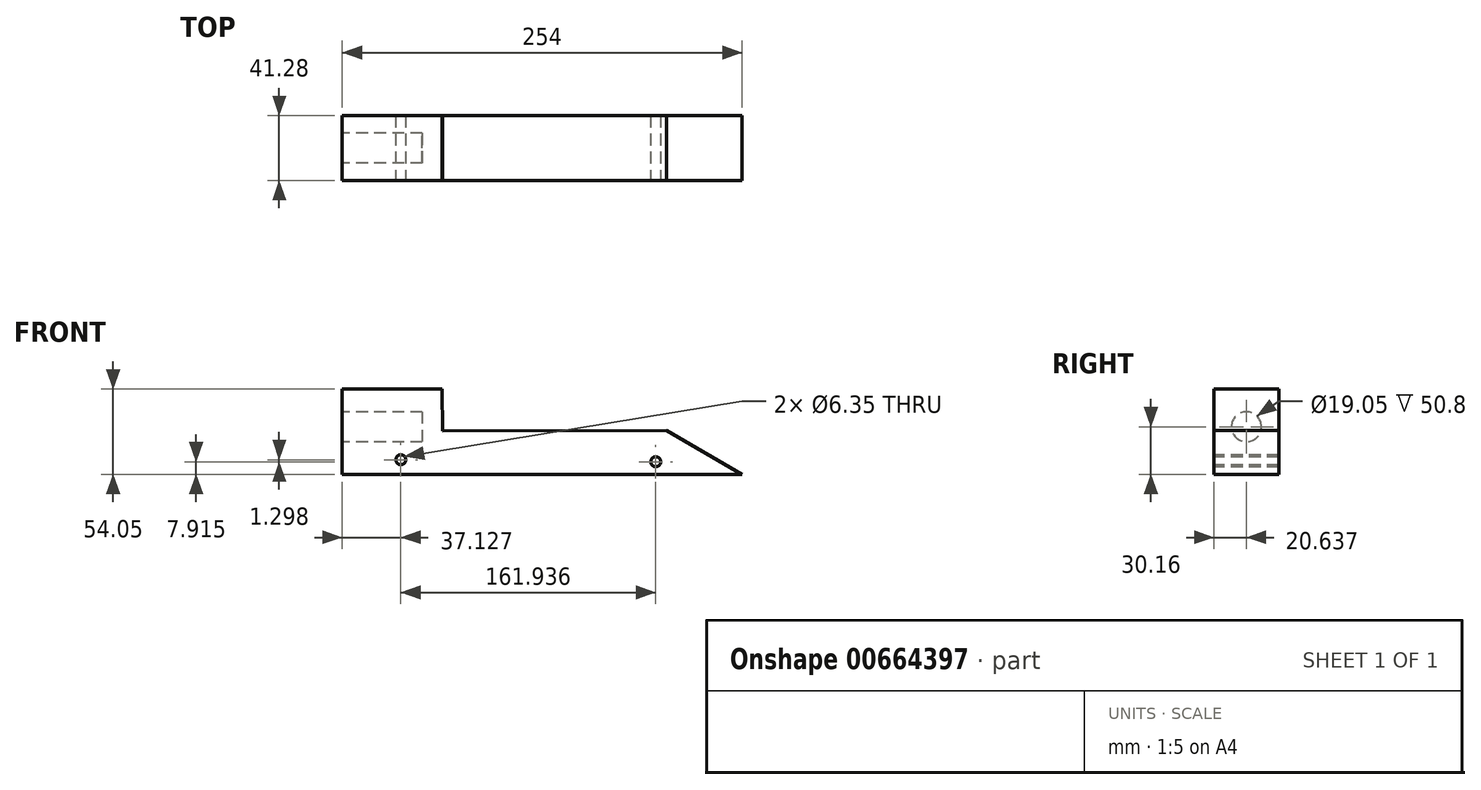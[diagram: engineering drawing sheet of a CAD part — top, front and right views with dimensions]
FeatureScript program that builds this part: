
annotation { "Feature Type Name" : "Feature", "Feature Type Description" : "" }
export const myFeature = defineFeature(function(context is Context, id is Id, definition is map)
    precondition{}
    {
        {
            var Q0;
            Q0=qCreatedBy(makeId("Front.planeOp"),FACE);
            var sketch = newSketch(context, id + "F0", { "sketchPlane" : qUnion([Q0])});
            skLineSegment(sketch, "E0", {"start": v(0, 73.03) * mm, "end": v(0, 0) * mm});
            skLineSegment(sketch, "E1", {"start": v(0, 0) * mm, "end": v(304.8, 0) * mm});
            skLineSegment(sketch, "E2", {"start": v(304.8, 0) * mm, "end": v(304.8, 19.05) * mm});
            skLineSegment(sketch, "E3", {"start": v(304.8, 19.05) * mm, "end": v(0, 73.03) * mm});
            skSolve(sketch);
        }
        {
            var Q0;
            Q0=makeQuery(id+"F0.imprint","IMPRINT",FACE,{"disambiguationData":[TD([[makeQuery(id+"F0.imprint","IMPRINT",EDGE,{"derivedFrom":sQuery(id+"F0.wireOp",EDGE,"E0")}),1.0]])]});
            extrude(context, id + "F1", {"entities" : qUnion([Q0]), "oppositeDirection" : true, "depth" : 41.27 * mm, "offsetDistance" : 25.4 * mm});
        }
        {
            var Q0;
            Q0=makeQuery(id+"F1.opExtrude","SWEPT_FACE",FACE,{"disambiguationData":[OSD([sQuery(id+"F0.wireOp",EDGE,"E0")])]});
            var sketch = newSketch(context, id + "F2", { "sketchPlane" : qUnion([Q0])});
            skCircle(sketch, "E4", {"center": v(-20.64, 30.16) * mm, "radius": 9.53 * mm});
            skSolve(sketch);
        }
        {
            var Q0;
            Q0 = qSketchRegion(id + "F2", true);
            extrude(context, id + "F3", {"entities" : qUnion([Q0]), "operationType" : NewBodyOperationType.REMOVE, "oppositeDirection" : true, "depth" : 50.8 * mm, "offsetDistance" : 25.4 * mm});
        }
        {
            var Q0;
            Q0=makeQuery(id+"F1.opExtrude","CAP_FACE",FACE,{"disambiguationData":[OSD([sQuery(id+"F0.wireOp",EDGE,"E0"),sQuery(id+"F0.wireOp",EDGE,"E1"),sQuery(id+"F0.wireOp",EDGE,"E2"),sQuery(id+"F0.wireOp",EDGE,"E3")])],"isStart":true});
            var sketch = newSketch(context, id + "F4", { "sketchPlane" : qUnion([Q0])});
            skLineSegment(sketch, "E5", {"start": v(0, 54.05) * mm, "end": v(107.16, 54.05) * mm});
            skLineSegment(sketch, "E6", {"start": v(0, 73.03) * mm, "end": v(107.16, 54.05) * mm});
            skLineSegment(sketch, "E7", {"start": v(107.16, 54.05) * mm, "end": v(120.44, 27.7) * mm});
            skLineSegment(sketch, "E8", {"start": v(120.44, 27.7) * mm, "end": v(253.72, 28.1) * mm});
            skLineSegment(sketch, "E9", {"start": v(253.72, 28.1) * mm, "end": v(304.8, 0) * mm});
            skSolve(sketch);
        }
        {
            var Q0;
            Q0 = qSketchRegion(id + "F4", true);
            var Q1;
            {var subQ0=sQuery(id+"F4.wireOp",EDGE,"E5");Q1=makeQuery(id+"F4.imprint","IMPRINT",FACE,{"disambiguationData":[TD([[makeQuery(id+"F4.imprint","IMPRINT",EDGE,{"derivedFrom":subQ0}),1.0]])]});}
            var Q2;
            {var subQ0=sQuery(id+"F4.wireOp",EDGE,"E7");Q2=makeQuery(id+"F4.imprint","IMPRINT",FACE,{"disambiguationData":[TD([[makeQuery(id+"F4.imprint","IMPRINT",EDGE,{"derivedFrom":subQ0}),1.0]])]});}
            var Q3;
            {var subQ0=sQuery(id+"F4.wireOp",EDGE,"E9");Q3=makeQuery(id+"F4.imprint","IMPRINT",FACE,{"disambiguationData":[TD([[makeQuery(id+"F4.imprint","IMPRINT",EDGE,{"derivedFrom":subQ0}),1.0]])]});}
            extrude(context, id + "F5", {"entities" : qUnion([Q0, Q1, Q2, Q3]), "operationType" : NewBodyOperationType.REMOVE, "oppositeDirection" : true, "depth" : 50.8 * mm, "offsetDistance" : 25.4 * mm});
        }
        {
            var Q0;
            Q0=makeQuery(id+"F1.opExtrude","CAP_FACE",FACE,{"disambiguationData":[OSD([sQuery(id+"F0.wireOp",EDGE,"E0"),sQuery(id+"F0.wireOp",EDGE,"E1"),sQuery(id+"F0.wireOp",EDGE,"E2"),sQuery(id+"F0.wireOp",EDGE,"E3")])],"isStart":true});
            var sketch = newSketch(context, id + "F6", { "sketchPlane" : qUnion([Q0])});
            skLineSegment(sketch, "E10", {"start": v(120.44, 27.7) * mm, "end": v(63.58, 27.53) * mm});
            skLineSegment(sketch, "E11", {"start": v(63.58, 27.53) * mm, "end": v(63.5, 54.05) * mm});
            skLineSegment(sketch, "E12", {"start": v(63.5, 54.05) * mm, "end": v(107.16, 54.05) * mm});
            skLineSegment(sketch, "E13", {"start": v(107.16, 54.05) * mm, "end": v(120.44, 27.7) * mm});
            skSolve(sketch);
        }
        {
            var Q0;
            Q0=makeQuery(id+"F6.imprint","IMPRINT",FACE,{"disambiguationData":[TD([[makeQuery(id+"F6.imprint","IMPRINT",EDGE,{"derivedFrom":sQuery(id+"F6.wireOp",EDGE,"E10")}),-1.0]])]});
            extrude(context, id + "F7", {"entities" : qUnion([Q0]), "operationType" : NewBodyOperationType.REMOVE, "oppositeDirection" : true, "depth" : 50.8 * mm, "offsetDistance" : 25.4 * mm});
        }
        {
            var Q0;
            Q0=makeQuery(id+"F1.opExtrude","CAP_FACE",FACE,{"disambiguationData":[OSD([sQuery(id+"F0.wireOp",EDGE,"E0"),sQuery(id+"F0.wireOp",EDGE,"E1"),sQuery(id+"F0.wireOp",EDGE,"E2"),sQuery(id+"F0.wireOp",EDGE,"E3")])],"isStart":true});
            var sketch = newSketch(context, id + "F8", { "sketchPlane" : qUnion([Q0])});
            skLineSegment(sketch, "E14", {"start": v(304.8, 0) * mm, "end": v(254, 0) * mm});
            skLineSegment(sketch, "E15", {"start": v(254, 0) * mm, "end": v(206.08, 27.95) * mm});
            skSolve(sketch);
        }
        {
            var Q0;
            Q0 = qSketchRegion(id + "F8", true);
            var Q1;
            Q1=makeQuery(id+"F8.imprint","IMPRINT",FACE,{"disambiguationData":[TD([[makeQuery(id+"F8.imprint","IMPRINT",EDGE,{"derivedFrom":sQuery(id+"F8.wireOp",EDGE,"E14")}),1.0]])]});
            extrude(context, id + "F9", {"entities" : qUnion([Q0, Q1]), "operationType" : NewBodyOperationType.REMOVE, "oppositeDirection" : true, "depth" : 50.8 * mm, "offsetDistance" : 25.4 * mm});
        }
        {
            var Q0;
            Q0=makeQuery(id+"F1.opExtrude","CAP_FACE",FACE,{"disambiguationData":[OSD([sQuery(id+"F0.wireOp",EDGE,"E0"),sQuery(id+"F0.wireOp",EDGE,"E1"),sQuery(id+"F0.wireOp",EDGE,"E2"),sQuery(id+"F0.wireOp",EDGE,"E3")])],"isStart":true});
            var sketch = newSketch(context, id + "F10", { "sketchPlane" : qUnion([Q0])});
            skCircle(sketch, "E16", {"center": v(37.13, 9.21) * mm, "radius": 3.18 * mm});
            skCircle(sketch, "E17", {"center": v(289.94, 6.52) * mm, "radius": 3.36 * mm});
            skCircle(sketch, "E18", {"center": v(199.06, 7.92) * mm, "radius": 3.18 * mm});
            skSolve(sketch);
        }
        {
            var Q0;
            Q0=makeQuery(id+"F10.imprint","IMPRINT",FACE,{"disambiguationData":[TD([[makeQuery(id+"F10.imprint","IMPRINT",EDGE,{"derivedFrom":sQuery(id+"F10.wireOp",EDGE,"E16")}),1.0]])]});
            var Q1;
            Q1=makeQuery(id+"F10.imprint","IMPRINT",FACE,{"disambiguationData":[TD([[makeQuery(id+"F10.imprint","IMPRINT",EDGE,{"derivedFrom":sQuery(id+"F10.wireOp",EDGE,"E17")}),1.0]])]});
            extrude(context, id + "F11", {"entities" : qUnion([Q0, Q1]), "operationType" : NewBodyOperationType.REMOVE, "oppositeDirection" : true, "depth" : 228.6 * mm, "offsetDistance" : 25.4 * mm});
        }
        {
            var Q0;
            Q0 = qSketchRegion(id + "F10", true);
            extrude(context, id + "F12", {"entities" : qUnion([Q0]), "operationType" : NewBodyOperationType.REMOVE, "oppositeDirection" : true, "depth" : 228.6 * mm, "offsetDistance" : 25.4 * mm});
        }
    });
